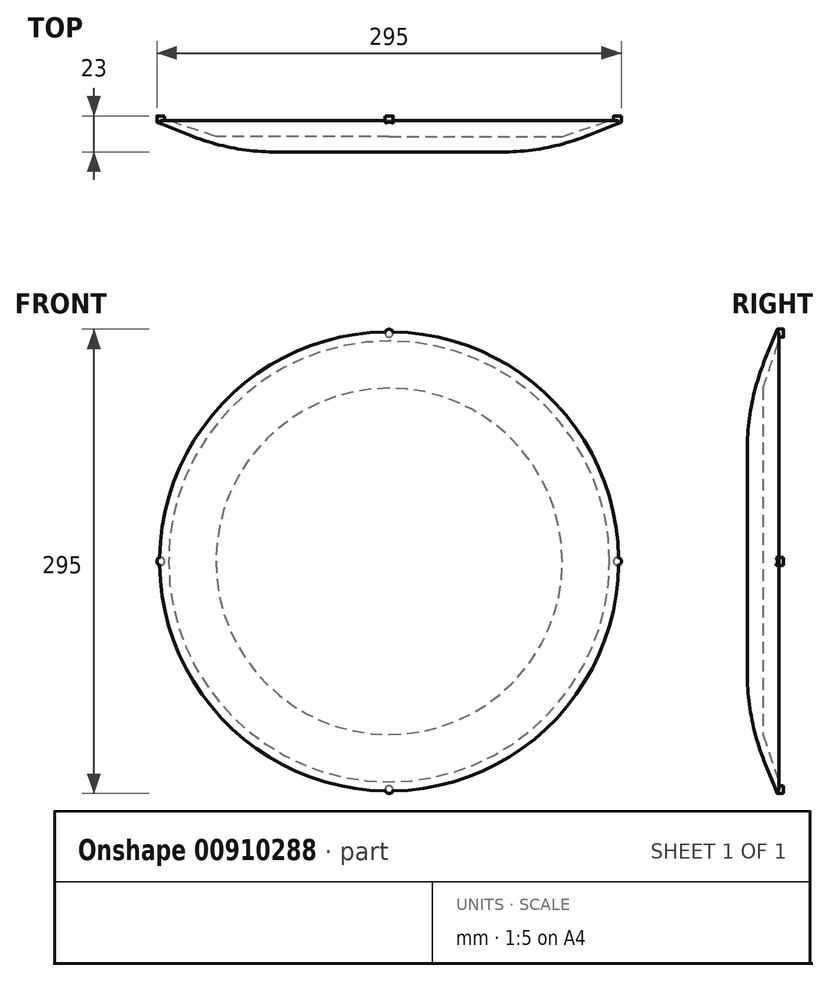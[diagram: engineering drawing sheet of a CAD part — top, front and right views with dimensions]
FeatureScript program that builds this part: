
annotation { "Feature Type Name" : "Feature", "Feature Type Description" : "" }
export const myFeature = defineFeature(function(context is Context, id is Id, definition is map)
    precondition{}
    {
        {
            var Q0;
            Q0=qCreatedBy(makeId("Front.planeOp"),FACE);
            var sketch = newSketch(context, id + "F0", { "sketchPlane" : qUnion([Q0])});
            skCircle(sketch, "E0", {"center": v(0, 0) * mm, "radius": 150 * mm});
            skSolve(sketch);
        }
        {
            var Q0;
            Q0=qCreatedBy(makeId("Front.planeOp"),FACE);
            cPlane(context, id + "F1", {"entities" : qUnion([Q0]), "cplaneType" : CPlaneType.OFFSET, "offset" : 20 * mm, "width" : 150 * mm, "height" : 150 * mm});
        }
        {
            var Q0;
            Q0=qCreatedBy(id+"F1.planeOp",FACE);
            var sketch = newSketch(context, id + "F2", { "sketchPlane" : qUnion([Q0])});
            skCircle(sketch, "E1", {"center": v(0, 0) * mm, "radius": 100 * mm});
            skSolve(sketch);
        }
        {
            var Q0;
            Q0=makeQuery(id+"F0.imprint","IMPRINT",FACE,{"disambiguationData":[TD([[makeQuery(id+"F0.imprint","IMPRINT",EDGE,{"derivedFrom":sQuery(id+"F0.wireOp",EDGE,"E0")}),1.0]])]});
            var Q1;
            Q1=makeQuery(id+"F2.imprint","IMPRINT",FACE,{"disambiguationData":[TD([[makeQuery(id+"F2.imprint","IMPRINT",EDGE,{"derivedFrom":sQuery(id+"F2.wireOp",EDGE,"E1")}),1.0]])]});
            loft(context, id + "F3", {"sheetProfilesArray" : [{ "sheetProfileEntities" : qUnion([Q0]) }, { "sheetProfileEntities" : qUnion([Q1]) }]});
        }
        {
            var Q0;
            Q0=makeQuery(id+"F3.opLoft","MID_CAP_EDGE",EDGE,{"disambiguationData":[OSD([sQuery(id+"F2.wireOp",EDGE,"E1")])],"capPos":1.0});
            fillet(context, id + "F4", {"entities" : qUnion([Q0]), "radius" : 150 * mm, "tangentPropagation" : true, "allowEdgeOverflow" : false});
        }
        {
            var Q0;
            Q0=makeQuery(id+"F3.opLoft","CAP_FACE",FACE,{"disambiguationData":[OSD([makeQuery(id+"F0.imprint","IMPRINT",FACE,{"disambiguationData":[TD([[makeQuery(id+"F0.imprint","IMPRINT",EDGE,{"derivedFrom":sQuery(id+"F0.wireOp",EDGE,"E0")}),1.0]])]})])],"isStart":true});
            var sketch = newSketch(context, id + "F5", { "sketchPlane" : qUnion([Q0])});
            skCircle(sketch, "E2", {"center": v(0, 0) * mm, "radius": 140 * mm});
            skSolve(sketch);
        }
        {
            var Q0;
            Q0=qCreatedBy(makeId("Front.planeOp"),FACE);
            cPlane(context, id + "F6", {"entities" : qUnion([Q0]), "cplaneType" : CPlaneType.OFFSET, "offset" : 10 * mm, "width" : 150 * mm, "height" : 150 * mm});
        }
        {
            var Q0;
            Q0=qCreatedBy(id+"F6.planeOp",FACE);
            var sketch = newSketch(context, id + "F7", { "sketchPlane" : qUnion([Q0])});
            skCircle(sketch, "E3", {"center": v(0, 0) * mm, "radius": 110 * mm});
            skSolve(sketch);
        }
        {
            var Q1;
            Q1=makeQuery(id+"F5.imprint","IMPRINT",FACE,{"disambiguationData":[TD([[makeQuery(id+"F5.imprint","IMPRINT",EDGE,{"derivedFrom":sQuery(id+"F5.wireOp",EDGE,"E2")}),1.0]])]});
            var Q2;
            Q2 = qSketchRegion(id + "F7", true);
            loft(context, id + "F8", {"operationType" : NewBodyOperationType.REMOVE, "sheetProfilesArray" : [{ "sheetProfileEntities" : qUnion([Q1]) }, { "sheetProfileEntities" : qUnion([Q2]) }]});
        }
        {
            var Q0;
            Q0=makeQuery(id+"F3.opLoft","CAP_FACE",FACE,{"disambiguationData":[OSD([makeQuery(id+"F0.imprint","IMPRINT",FACE,{"disambiguationData":[TD([[makeQuery(id+"F0.imprint","IMPRINT",EDGE,{"derivedFrom":sQuery(id+"F0.wireOp",EDGE,"E0")}),1.0]])]})])],"isStart":true});
            var sketch = newSketch(context, id + "F9", { "sketchPlane" : qUnion([Q0])});
            skCircle(sketch, "E4", {"center": v(0, 145) * mm, "radius": 2.5 * mm});
            skCircle(sketch, "E5", {"center": v(-145, 0) * mm, "radius": 2.5 * mm});
            skCircle(sketch, "E6", {"center": v(145, 0) * mm, "radius": 2.5 * mm});
            skCircle(sketch, "E7", {"center": v(0, -145) * mm, "radius": 2.5 * mm});
            skSolve(sketch);
        }
        {
            var Q0;
            Q0 = qSketchRegion(id + "F9", true);
            extrude(context, id + "F10", {"entities" : qUnion([Q0]), "operationType" : NewBodyOperationType.ADD, "depth" : 3 * mm, "offsetDistance" : 25 * mm});
        }
        {
            var Q0;
            Q0=makeQuery(id+"F3.opLoft","MID_CAP_EDGE",EDGE,{"disambiguationData":[OSD([sQuery(id+"F0.wireOp",EDGE,"E0")])],"capPos":0.0});
            fillet(context, id + "F11", {"entities" : qUnion([Q0]), "radius" : 1 * mm, "tangentPropagation" : true, "allowEdgeOverflow" : false});
        }
    });
